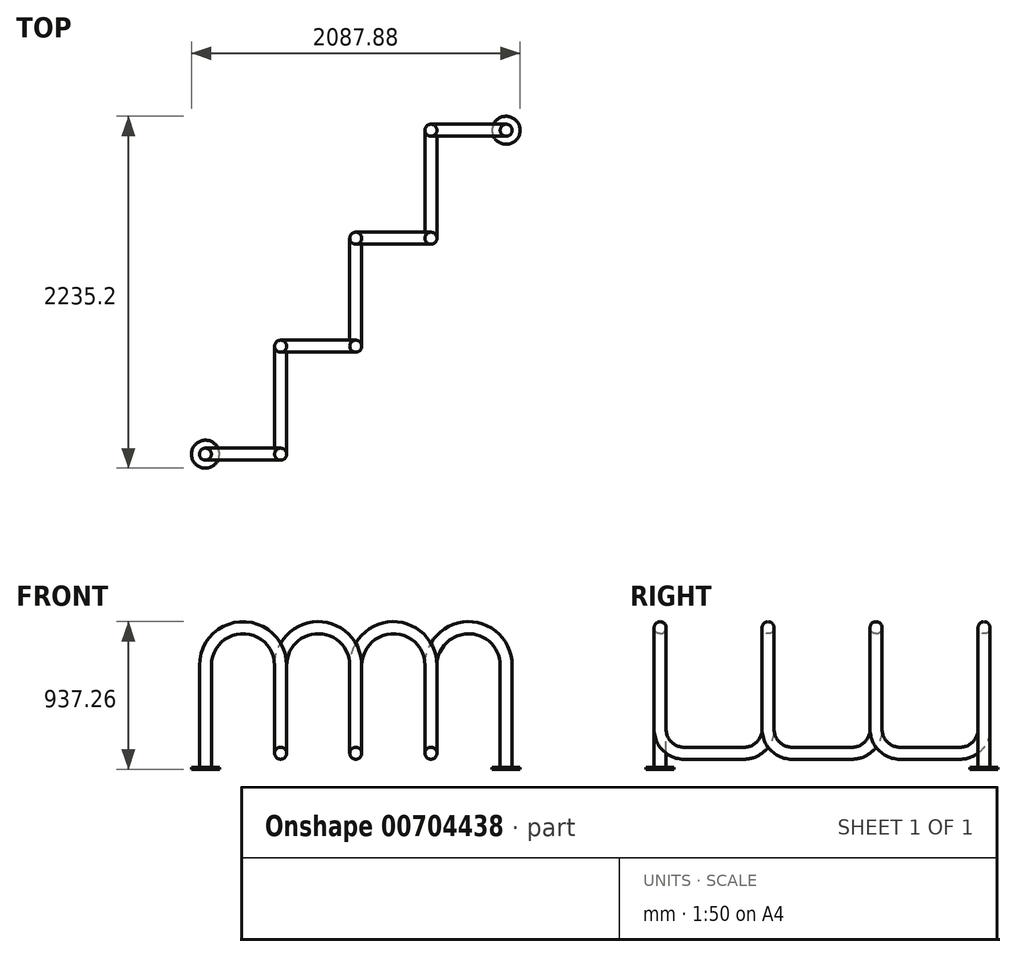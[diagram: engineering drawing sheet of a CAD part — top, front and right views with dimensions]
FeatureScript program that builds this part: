
annotation { "Feature Type Name" : "Feature", "Feature Type Description" : "" }
export const myFeature = defineFeature(function(context is Context, id is Id, definition is map)
    precondition{}
    {
        {
            var Q0;
            Q0=qCreatedBy(makeId("Top.planeOp"),FACE);
            var sketch = newSketch(context, id + "F0", { "sketchPlane" : qUnion([Q0])});
            skCircle(sketch, "E0", {"center": v(0, 0) * mm, "radius": 38.1 * mm});
            skCircle(sketch, "E1", {"center": v(0, 0) * mm, "radius": 88.9 * mm});
            skSolve(sketch);
        }
        {
            var Q0;
            Q0=qCreatedBy(makeId("Front.planeOp"),FACE);
            var sketch = newSketch(context, id + "F1", { "sketchPlane" : qUnion([Q0])});
            skLineSegment(sketch, "E2", {"start": v(0, 0) * mm, "end": v(0, 660.4) * mm});
            skArc(sketch, "E3", {"start": v(477.52, 660.4) * mm, "mid": v(238.76, 899.16) * mm, "end": v(0, 660.4) * mm});
            skLineSegment(sketch, "E4", {"start": v(477.52, 660.4) * mm, "end": v(477.52, 254) * mm});
            skSolve(sketch);
        }
        {
            var Q0;
            Q0=sQuery(id+"F1.wireOp",EDGE,"E4");
            cPlane(context, id + "F2", {"entities" : qUnion([Q0]), "cplaneType" : CPlaneType.LINE_ANGLE, "offset" : 25.4 * mm, "angle" : 0 * degree, "width" : 152.4 * mm, "height" : 152.4 * mm});
        }
        {
            var Q0;
            Q0=qCreatedBy(id+"F2.planeOp",FACE);
            var sketch = newSketch(context, id + "F3", { "sketchPlane" : qUnion([Q0])});
            skArc(sketch, "E5", {"start": v(0, 254) * mm, "mid": v(-44.64, 146.24) * mm, "end": v(-152.4, 101.6) * mm});
            skLineSegment(sketch, "E6", {"start": v(-152.4, 101.6) * mm, "end": v(-533.4, 101.6) * mm});
            skArc(sketch, "E7", {"start": v(-533.4, 101.6) * mm, "mid": v(-641.16, 146.24) * mm, "end": v(-685.8, 254) * mm});
            skLineSegment(sketch, "E8", {"start": v(-685.8, 254) * mm, "end": v(-685.8, 660.4) * mm});
            skSolve(sketch);
        }
        {
            var Q0;
            Q0=sQuery(id+"F3.wireOp",EDGE,"E8");
            cPlane(context, id + "F4", {"entities" : qUnion([Q0]), "cplaneType" : CPlaneType.LINE_ANGLE, "offset" : 25.4 * mm, "angle" : 90 * degree, "width" : 152.4 * mm, "height" : 152.4 * mm});
        }
        {
            var Q0;
            Q0=qCreatedBy(id+"F4.planeOp",FACE);
            var sketch = newSketch(context, id + "F5", { "sketchPlane" : qUnion([Q0])});
            skArc(sketch, "E9", {"start": v(-477.52, 660.4) * mm, "mid": v(-716.28, 899.16) * mm, "end": v(-955.04, 660.4) * mm});
            skLineSegment(sketch, "E10", {"start": v(-955.04, 660.4) * mm, "end": v(-955.04, 254) * mm});
            skSolve(sketch);
        }
        {
            var Q0;
            Q0=sQuery(id+"F5.wireOp",EDGE,"E10");
            cPlane(context, id + "F6", {"entities" : qUnion([Q0]), "cplaneType" : CPlaneType.LINE_ANGLE, "offset" : 25.4 * mm, "angle" : 0 * degree, "width" : 152.4 * mm, "height" : 152.4 * mm});
        }
        {
            var Q0;
            Q0=qCreatedBy(id+"F6.planeOp",FACE);
            var sketch = newSketch(context, id + "F7", { "sketchPlane" : qUnion([Q0])});
            skArc(sketch, "E11", {"start": v(-685.8, 254) * mm, "mid": v(-730.44, 146.24) * mm, "end": v(-838.2, 101.6) * mm});
            skArc(sketch, "E12", {"start": v(-1371.6, 254) * mm, "mid": v(-1326.96, 146.24) * mm, "end": v(-1219.2, 101.6) * mm});
            skLineSegment(sketch, "E13", {"start": v(-838.2, 101.6) * mm, "end": v(-1219.2, 101.6) * mm});
            skLineSegment(sketch, "E14", {"start": v(-1371.6, 254) * mm, "end": v(-1371.6, 660.4) * mm});
            skSolve(sketch);
        }
        {
            var Q0;
            Q0=sQuery(id+"F7.wireOp",EDGE,"E14");
            cPlane(context, id + "F8", {"entities" : qUnion([Q0]), "cplaneType" : CPlaneType.LINE_ANGLE, "offset" : 25.4 * mm, "angle" : 90 * degree, "width" : 152.4 * mm, "height" : 152.4 * mm});
        }
        {
            var Q0;
            Q0=qCreatedBy(id+"F8.planeOp",FACE);
            var sketch = newSketch(context, id + "F9", { "sketchPlane" : qUnion([Q0])});
            skArc(sketch, "E15", {"start": v(-955.04, 660.4) * mm, "mid": v(-1193.8, 899.16) * mm, "end": v(-1432.56, 660.4) * mm});
            skLineSegment(sketch, "E16", {"start": v(-1432.56, 660.4) * mm, "end": v(-1432.56, 254) * mm});
            skSolve(sketch);
        }
        {
            var Q0;
            Q0=sQuery(id+"F9.wireOp",EDGE,"E16");
            cPlane(context, id + "F10", {"entities" : qUnion([Q0]), "cplaneType" : CPlaneType.LINE_ANGLE, "offset" : 25.4 * mm, "angle" : 0 * degree, "width" : 152.4 * mm, "height" : 152.4 * mm});
        }
        {
            var Q0;
            Q0=qCreatedBy(id+"F10.planeOp",FACE);
            var sketch = newSketch(context, id + "F11", { "sketchPlane" : qUnion([Q0])});
            skArc(sketch, "E17", {"start": v(-1371.6, 254) * mm, "mid": v(-1416.24, 146.24) * mm, "end": v(-1524, 101.6) * mm});
            skArc(sketch, "E18", {"start": v(-1905, 101.6) * mm, "mid": v(-2012.76, 146.24) * mm, "end": v(-2057.4, 254) * mm});
            skLineSegment(sketch, "E19", {"start": v(-1524, 101.6) * mm, "end": v(-1905, 101.6) * mm});
            skLineSegment(sketch, "E20", {"start": v(-2057.4, 254) * mm, "end": v(-2057.4, 660.4) * mm});
            skSolve(sketch);
        }
        {
            var Q0;
            Q0=sQuery(id+"F11.wireOp",EDGE,"E20");
            cPlane(context, id + "F12", {"entities" : qUnion([Q0]), "cplaneType" : CPlaneType.LINE_ANGLE, "offset" : 25.4 * mm, "angle" : 90 * degree, "width" : 152.4 * mm, "height" : 152.4 * mm});
        }
        {
            var Q0;
            Q0=qCreatedBy(id+"F12.planeOp",FACE);
            var sketch = newSketch(context, id + "F13", { "sketchPlane" : qUnion([Q0])});
            skArc(sketch, "E21", {"start": v(-1432.56, 660.4) * mm, "mid": v(-1671.32, 899.16) * mm, "end": v(-1910.08, 660.4) * mm});
            skLineSegment(sketch, "E22", {"start": v(-1910.08, 660.4) * mm, "end": v(-1910.08, 0) * mm});
            skSolve(sketch);
        }
        {
            var Q0;
            Q0=qCreatedBy(makeId("Top.planeOp"),FACE);
            var sketch = newSketch(context, id + "F14", { "sketchPlane" : qUnion([Q0])});
            skCircle(sketch, "E23", {"center": v(1910.08, 2057.4) * mm, "radius": 38.1 * mm});
            skCircle(sketch, "E24", {"center": v(1910.08, 2057.4) * mm, "radius": 88.9 * mm});
            skSolve(sketch);
        }
        {
            var Q0;
            Q0=makeQuery(id+"F0.imprint","IMPRINT",FACE,{"disambiguationData":[TD([[makeQuery(id+"F0.imprint","IMPRINT",EDGE,{"derivedFrom":sQuery(id+"F0.wireOp",EDGE,"E0")}),1.0]])]});
            var Q1;
            Q1=sQuery(id+"F1.wireOp",EDGE,"E2");
            var Q2;
            Q2=sQuery(id+"F1.wireOp",EDGE,"E3");
            var Q3;
            Q3=sQuery(id+"F1.wireOp",EDGE,"E4");
            var Q4;
            Q4=sQuery(id+"F3.wireOp",EDGE,"E5");
            var Q5;
            Q5=sQuery(id+"F3.wireOp",EDGE,"E6");
            var Q6;
            Q6=sQuery(id+"F3.wireOp",EDGE,"E7");
            var Q7;
            Q7=sQuery(id+"F3.wireOp",EDGE,"E8");
            var Q8;
            Q8=sQuery(id+"F5.wireOp",EDGE,"E9");
            var Q9;
            Q9=sQuery(id+"F5.wireOp",EDGE,"E10");
            var Q10;
            Q10=sQuery(id+"F7.wireOp",EDGE,"E11");
            var Q11;
            Q11=sQuery(id+"F7.wireOp",EDGE,"E13");
            var Q12;
            Q12=sQuery(id+"F7.wireOp",EDGE,"E12");
            var Q13;
            Q13=sQuery(id+"F7.wireOp",EDGE,"E14");
            var Q14;
            Q14=sQuery(id+"F9.wireOp",EDGE,"E15");
            var Q15;
            Q15=sQuery(id+"F9.wireOp",EDGE,"E16");
            var Q16;
            Q16=sQuery(id+"F11.wireOp",EDGE,"E17");
            var Q17;
            Q17=sQuery(id+"F11.wireOp",EDGE,"E19");
            var Q18;
            Q18=sQuery(id+"F11.wireOp",EDGE,"E18");
            var Q19;
            Q19=sQuery(id+"F11.wireOp",EDGE,"E20");
            var Q20;
            Q20=sQuery(id+"F13.wireOp",EDGE,"E21");
            var Q21;
            Q21=sQuery(id+"F13.wireOp",EDGE,"E22");
            sweep(context, id + "F15", {"profiles" : qUnion([Q0]), "path" : qUnion([Q1, Q2, Q3, Q4, Q5, Q6, Q7, Q8, Q9, Q10, Q11, Q12, Q13, Q14, Q15, Q16, Q17, Q18, Q19, Q20, Q21])});
        }
        {
            var Q0;
            Q0=makeQuery(id+"F0.imprint","IMPRINT",FACE,{"disambiguationData":[TD([[makeQuery(id+"F0.imprint","IMPRINT",EDGE,{"derivedFrom":sQuery(id+"F0.wireOp",EDGE,"E0")}),-1.0]])]});
            extrude(context, id + "F16", {"entities" : qUnion([Q0]), "operationType" : NewBodyOperationType.ADD, "depth" : 12.7 * mm, "offsetDistance" : 25.4 * mm});
        }
        {
            var Q0;
            Q0=makeQuery(id+"F14.imprint","IMPRINT",FACE,{"disambiguationData":[TD([[makeQuery(id+"F14.imprint","IMPRINT",EDGE,{"derivedFrom":sQuery(id+"F14.wireOp",EDGE,"E23")}),-1.0]])]});
            extrude(context, id + "F17", {"entities" : qUnion([Q0]), "operationType" : NewBodyOperationType.ADD, "depth" : 12.7 * mm, "offsetDistance" : 25.4 * mm});
        }
    });
